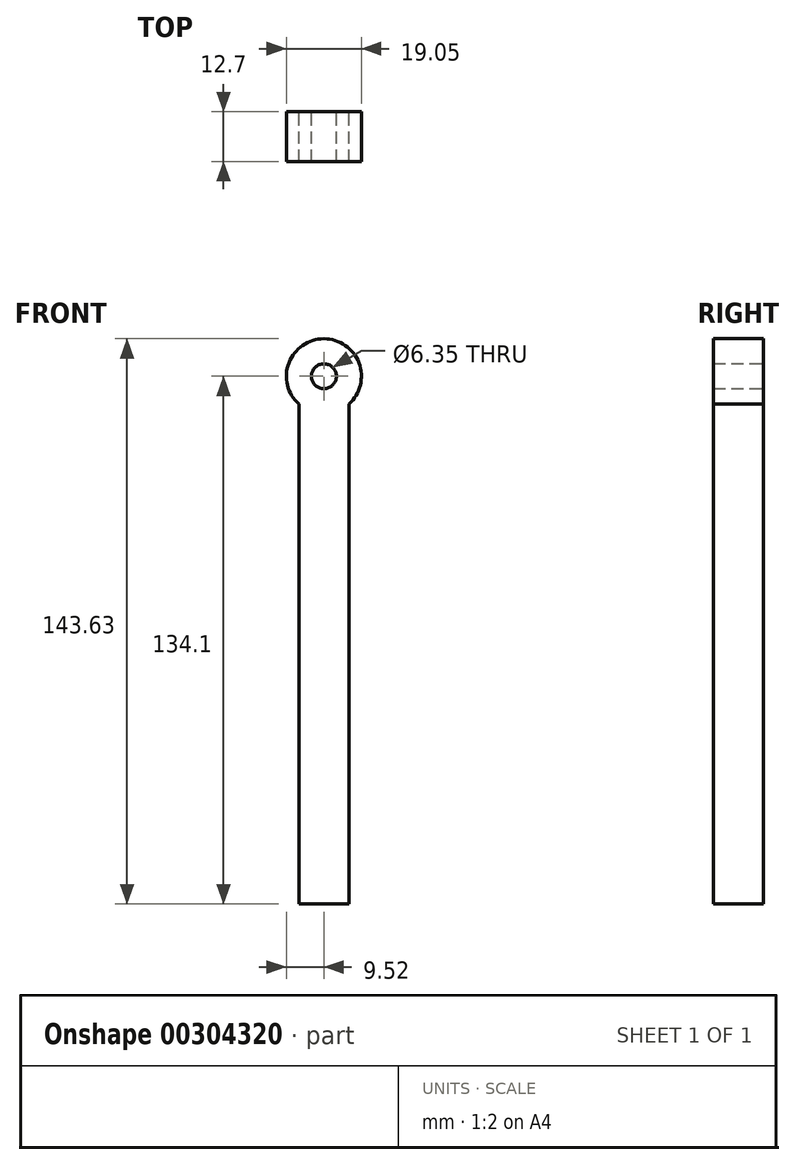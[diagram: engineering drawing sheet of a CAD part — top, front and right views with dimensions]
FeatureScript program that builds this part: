
annotation { "Feature Type Name" : "Feature", "Feature Type Description" : "" }
export const myFeature = defineFeature(function(context is Context, id is Id, definition is map)
    precondition{}
    {
        {
            var Q0;
            Q0=qCreatedBy(makeId("Front.planeOp"),FACE);
            var sketch = newSketch(context, id + "F0", { "sketchPlane" : qUnion([Q0])});
            skArc(sketch, "E0", {"start": v(6.35, -7.1) * mm, "mid": v(0, 9.52) * mm, "end": v(-6.35, -7.1) * mm});
            skCircle(sketch, "E1", {"center": v(0, 0) * mm, "radius": 3.18 * mm});
            skLineSegment(sketch, "E2.top", {"start": v(-6.35, -134.1) * mm, "end": v(6.35, -134.1) * mm});
            skLineSegment(sketch, "E2.left", {"start": v(-6.35, -7.1) * mm, "end": v(-6.35, -134.1) * mm});
            skLineSegment(sketch, "E2.right", {"start": v(6.35, -7.1) * mm, "end": v(6.35, -134.1) * mm});
            skSolve(sketch);
        }
        {
            var Q0;
            Q0=makeQuery(id+"F0.imprint","IMPRINT",FACE,{"disambiguationData":[TD([[makeQuery(id+"F0.imprint","IMPRINT",EDGE,{"derivedFrom":sQuery(id+"F0.wireOp",EDGE,"E0")}),1.0]])]});
            extrude(context, id + "F1", {"entities" : qUnion([Q0]), "depth" : 12.7 * mm});
        }
    });
